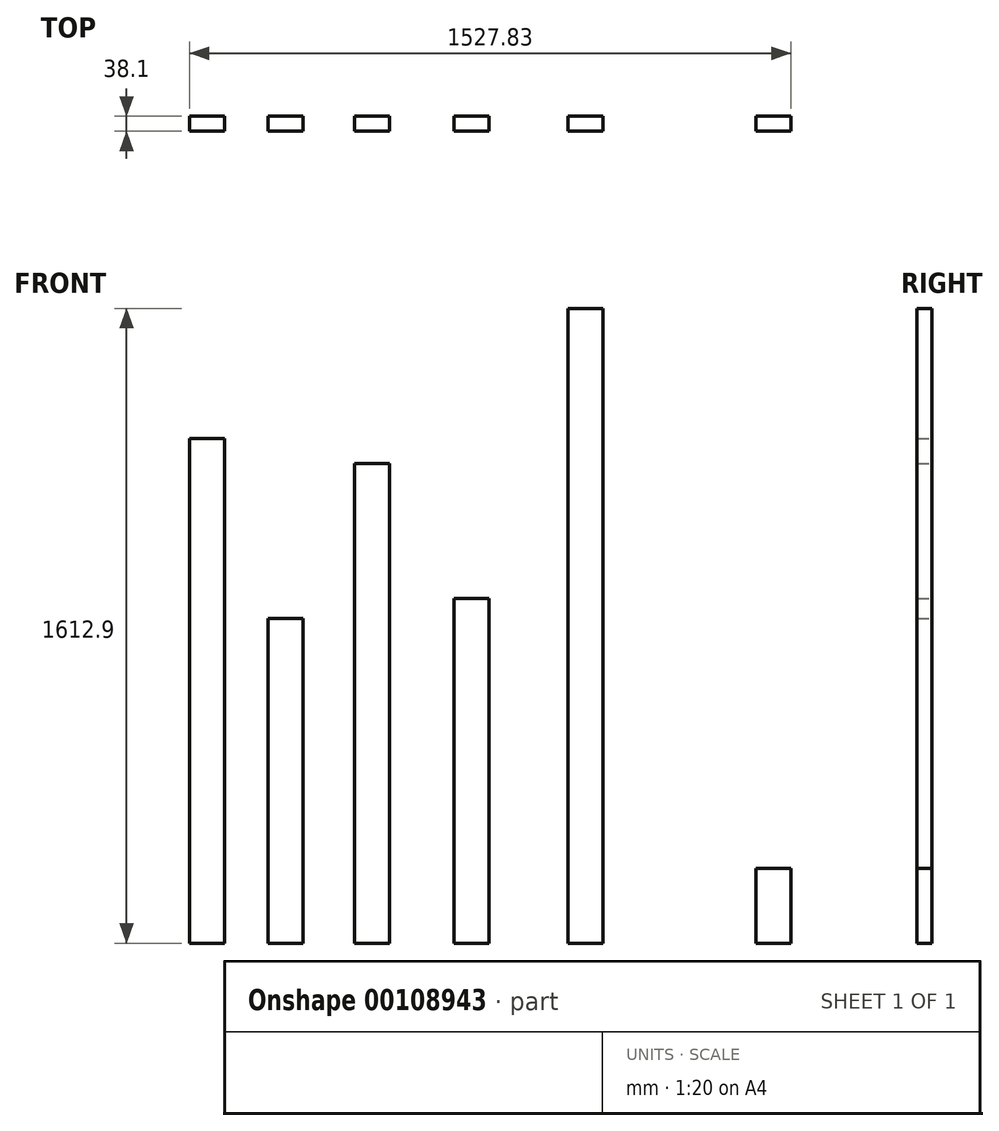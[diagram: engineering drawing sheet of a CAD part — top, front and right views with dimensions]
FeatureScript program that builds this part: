
annotation { "Feature Type Name" : "Feature", "Feature Type Description" : "" }
export const myFeature = defineFeature(function(context is Context, id is Id, definition is map)
    precondition{}
    {
        {
            var Q0;
            Q0=qCreatedBy(makeId("Top.planeOp"),FACE);
            var sketch = newSketch(context, id + "F0", { "sketchPlane" : qUnion([Q0])});
            skLineSegment(sketch, "E0.bottom", {"start": v(44.45, -19.05) * mm, "end": v(-44.45, -19.05) * mm});
            skLineSegment(sketch, "E0.top", {"start": v(44.45, 19.05) * mm, "end": v(-44.45, 19.05) * mm});
            skLineSegment(sketch, "E0.left", {"start": v(44.45, -19.05) * mm, "end": v(44.45, 19.05) * mm});
            skLineSegment(sketch, "E0.right", {"start": v(-44.45, -19.05) * mm, "end": v(-44.45, 19.05) * mm});
            skPoint(sketch, "E0.middle", {"position": v(0, 0) * mm});
            skSolve(sketch);
        }
        {
            var Q0;
            Q0=makeQuery(id+"F0.imprint","IMPRINT",FACE,{"disambiguationData":[TD([[makeQuery(id+"F0.imprint","IMPRINT",EDGE,{"derivedFrom":sQuery(id+"F0.wireOp",EDGE,"E0.bottom")}),-1.0]])]});
            extrude(context, id + "F1", {"entities" : qUnion([Q0]), "depth" : 876.3 * mm});
        }
        {
            var Q0;
            Q0=qCreatedBy(makeId("Top.planeOp"),FACE);
            var sketch = newSketch(context, id + "F2", { "sketchPlane" : qUnion([Q0])});
            skLineSegment(sketch, "E1.bottom", {"start": v(-208.1, -19.05) * mm, "end": v(-297, -19.05) * mm});
            skLineSegment(sketch, "E1.top", {"start": v(-208.1, 19.05) * mm, "end": v(-297, 19.05) * mm});
            skLineSegment(sketch, "E1.left", {"start": v(-208.1, -19.05) * mm, "end": v(-208.1, 19.05) * mm});
            skLineSegment(sketch, "E1.right", {"start": v(-297, -19.05) * mm, "end": v(-297, 19.05) * mm});
            skPoint(sketch, "E1.middle", {"position": v(-252.55, 0) * mm});
            skSolve(sketch);
        }
        {
            var Q0;
            Q0=makeQuery(id+"F2.imprint","IMPRINT",FACE,{"disambiguationData":[TD([[makeQuery(id+"F2.imprint","IMPRINT",EDGE,{"derivedFrom":sQuery(id+"F2.wireOp",EDGE,"E1.bottom")}),-1.0]])]});
            extrude(context, id + "F3", {"entities" : qUnion([Q0]), "depth" : 1219.2 * mm});
        }
        {
            var Q0;
            Q0=qCreatedBy(makeId("Top.planeOp"),FACE);
            var sketch = newSketch(context, id + "F4", { "sketchPlane" : qUnion([Q0])});
            skLineSegment(sketch, "E2.bottom", {"start": v(245.66, -19.05) * mm, "end": v(334.56, -19.05) * mm});
            skLineSegment(sketch, "E2.top", {"start": v(245.66, 19.05) * mm, "end": v(334.56, 19.05) * mm});
            skLineSegment(sketch, "E2.left", {"start": v(245.66, -19.05) * mm, "end": v(245.66, 19.05) * mm});
            skLineSegment(sketch, "E2.right", {"start": v(334.56, -19.05) * mm, "end": v(334.56, 19.05) * mm});
            skPoint(sketch, "E2.middle", {"position": v(290.11, 0) * mm});
            skSolve(sketch);
        }
        {
            var Q0;
            Q0=makeQuery(id+"F4.imprint","IMPRINT",FACE,{"disambiguationData":[TD([[makeQuery(id+"F4.imprint","IMPRINT",EDGE,{"derivedFrom":sQuery(id+"F4.wireOp",EDGE,"E2.bottom")}),1.0]])]});
            extrude(context, id + "F5", {"entities" : qUnion([Q0]), "depth" : 1612.9 * mm});
        }
        {
            var Q0;
            Q0=qCreatedBy(makeId("Top.planeOp"),FACE);
            var sketch = newSketch(context, id + "F6", { "sketchPlane" : qUnion([Q0])});
            skLineSegment(sketch, "E3.bottom", {"start": v(-427.6, -19.05) * mm, "end": v(-516.5, -19.05) * mm});
            skLineSegment(sketch, "E3.top", {"start": v(-427.6, 19.05) * mm, "end": v(-516.5, 19.05) * mm});
            skLineSegment(sketch, "E3.left", {"start": v(-427.6, -19.05) * mm, "end": v(-427.6, 19.05) * mm});
            skLineSegment(sketch, "E3.right", {"start": v(-516.5, -19.05) * mm, "end": v(-516.5, 19.05) * mm});
            skPoint(sketch, "E3.middle", {"position": v(-472.05, 0) * mm});
            skSolve(sketch);
        }
        {
            var Q0;
            Q0=makeQuery(id+"F6.imprint","IMPRINT",FACE,{"disambiguationData":[TD([[makeQuery(id+"F6.imprint","IMPRINT",EDGE,{"derivedFrom":sQuery(id+"F6.wireOp",EDGE,"E3.bottom")}),-1.0]])]});
            extrude(context, id + "F7", {"entities" : qUnion([Q0]), "depth" : 825.5 * mm});
        }
        {
            var Q0;
            Q0=qCreatedBy(makeId("Top.planeOp"),FACE);
            var sketch = newSketch(context, id + "F8", { "sketchPlane" : qUnion([Q0])});
            skLineSegment(sketch, "E4.bottom", {"start": v(811.46, -19.05) * mm, "end": v(722.56, -19.05) * mm});
            skLineSegment(sketch, "E4.top", {"start": v(811.46, 19.05) * mm, "end": v(722.56, 19.05) * mm});
            skLineSegment(sketch, "E4.left", {"start": v(811.46, -19.05) * mm, "end": v(811.46, 19.05) * mm});
            skLineSegment(sketch, "E4.right", {"start": v(722.56, -19.05) * mm, "end": v(722.56, 19.05) * mm});
            skPoint(sketch, "E4.middle", {"position": v(767.01, 0) * mm});
            skSolve(sketch);
        }
        {
            var Q0;
            Q0=makeQuery(id+"F8.imprint","IMPRINT",FACE,{"disambiguationData":[TD([[makeQuery(id+"F8.imprint","IMPRINT",EDGE,{"derivedFrom":sQuery(id+"F8.wireOp",EDGE,"E4.bottom")}),-1.0]])]});
            extrude(context, id + "F9", {"entities" : qUnion([Q0]), "depth" : 190.5 * mm});
        }
        {
            var Q0;
            Q0=qCreatedBy(makeId("Top.planeOp"),FACE);
            var sketch = newSketch(context, id + "F10", { "sketchPlane" : qUnion([Q0])});
            skLineSegment(sketch, "E5.bottom", {"start": v(-627.47, -19.05) * mm, "end": v(-716.37, -19.05) * mm});
            skLineSegment(sketch, "E5.top", {"start": v(-627.47, 19.05) * mm, "end": v(-716.37, 19.05) * mm});
            skLineSegment(sketch, "E5.left", {"start": v(-627.47, -19.05) * mm, "end": v(-627.47, 19.05) * mm});
            skLineSegment(sketch, "E5.right", {"start": v(-716.37, -19.05) * mm, "end": v(-716.37, 19.05) * mm});
            skPoint(sketch, "E5.middle", {"position": v(-671.92, 0) * mm});
            skSolve(sketch);
        }
        {
            var Q0;
            Q0=makeQuery(id+"F10.imprint","IMPRINT",FACE,{"disambiguationData":[TD([[makeQuery(id+"F10.imprint","IMPRINT",EDGE,{"derivedFrom":sQuery(id+"F10.wireOp",EDGE,"E5.bottom")}),-1.0]])]});
            extrude(context, id + "F11", {"entities" : qUnion([Q0]), "depth" : 1282.7 * mm});
        }
    });
